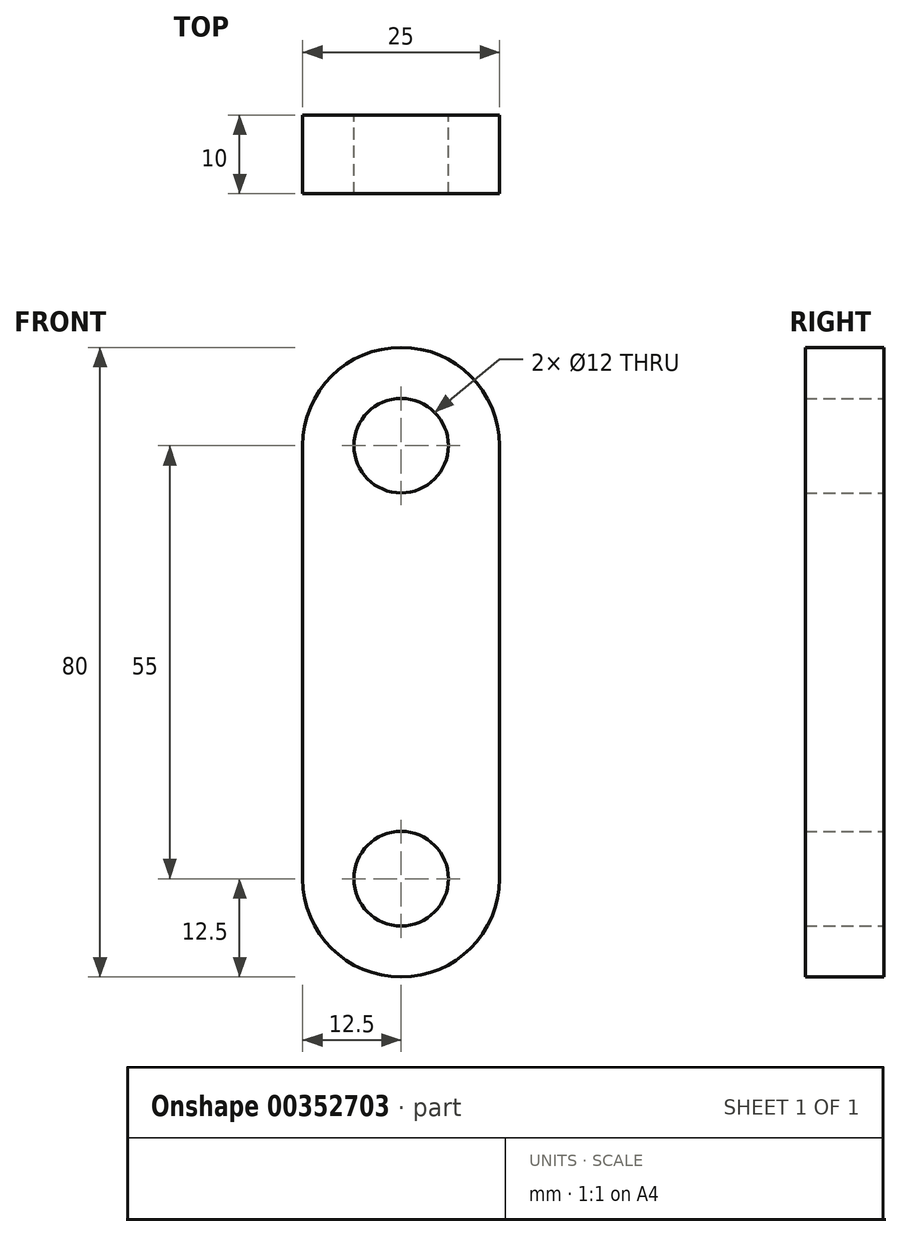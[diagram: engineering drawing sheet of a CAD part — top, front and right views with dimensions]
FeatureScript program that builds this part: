
annotation { "Feature Type Name" : "Feature", "Feature Type Description" : "" }
export const myFeature = defineFeature(function(context is Context, id is Id, definition is map)
    precondition{}
    {
        {
            var Q0;
            Q0=qCreatedBy(makeId("Front.planeOp"),FACE);
            var sketch = newSketch(context, id + "F0", { "sketchPlane" : qUnion([Q0])});
            skLineSegment(sketch, "E0.bottom", {"start": v(0, -40) * mm, "end": v(0, -40) * mm});
            skLineSegment(sketch, "E0.top", {"start": v(0, 40) * mm, "end": v(0, 40) * mm});
            skLineSegment(sketch, "E0.left", {"start": v(12.5, -27.5) * mm, "end": v(12.5, 27.5) * mm});
            skLineSegment(sketch, "E0.right", {"start": v(-12.5, -27.5) * mm, "end": v(-12.5, 27.5) * mm});
            skPoint(sketch, "E0.middle", {"position": v(0, 0) * mm});
            skPoint(sketch, "E1.visualSharp", {"position": v(-12.5, 40) * mm});
            skArc(sketch, "E1.filletArc", {"start": v(0, 40) * mm, "mid": v(-8.84, 36.34) * mm, "end": v(-12.5, 27.5) * mm});
            skPoint(sketch, "E2.visualSharp", {"position": v(12.5, 40) * mm});
            skArc(sketch, "E2.filletArc", {"start": v(12.5, 27.5) * mm, "mid": v(8.84, 36.34) * mm, "end": v(0, 40) * mm});
            skPoint(sketch, "E3.visualSharp", {"position": v(12.5, -40) * mm});
            skArc(sketch, "E3.filletArc", {"start": v(0, -40) * mm, "mid": v(8.84, -36.34) * mm, "end": v(12.5, -27.5) * mm});
            skPoint(sketch, "E4.visualSharp", {"position": v(-12.5, -40) * mm});
            skArc(sketch, "E4.filletArc", {"start": v(-12.5, -27.5) * mm, "mid": v(-8.84, -36.34) * mm, "end": v(0, -40) * mm});
            skLineSegment(sketch, "E5", {"start": v(-4.51, 27.5) * mm, "end": v(5.8, 27.5) * mm});
            skLineSegment(sketch, "E6", {"start": v(-4.85, -27.5) * mm, "end": v(5.58, -27.5) * mm});
            skSolve(sketch);
        }
        {
            var Q0;
            Q0 = qSketchRegion(id + "F0", true);
            extrude(context, id + "F1", {"entities" : qUnion([Q0]), "depth" : 10 * mm});
        }
        {
            var Q0;
            Q0=sQuery(id+"F0.wireOp",VERTEX,"E1.filletArc.center");
            var Q1;
            Q1=sQuery(id+"F0.wireOp",VERTEX,"E3.filletArc.center");
            var Q2;
            Q2=makeQuery(id+"F1.opExtrude","SWEPT_BODY",BODY,{"disambiguationData":[OSD([sQuery(id+"F0.wireOp",EDGE,"E0.left"),sQuery(id+"F0.wireOp",EDGE,"E0.right"),sQuery(id+"F0.wireOp",EDGE,"E1.filletArc"),sQuery(id+"F0.wireOp",EDGE,"E2.filletArc"),sQuery(id+"F0.wireOp",EDGE,"E3.filletArc"),sQuery(id+"F0.wireOp",EDGE,"E4.filletArc")])]});
            hole(context, id + "F2", {"style" : HoleStyle.SIMPLE, "endStyle" : HoleEndStyle.BLIND, "oppositeDirection" : true, "holeDiameter" : 12 * mm, "holeDepth" : 30 * mm, "isTappedThrough" : true, "tappedDepth" : 12 * mm, "tapClearance" : 3, "locations" : qUnion([Q0, Q1]), "scope" : qUnion([Q2])});
        }
    });
